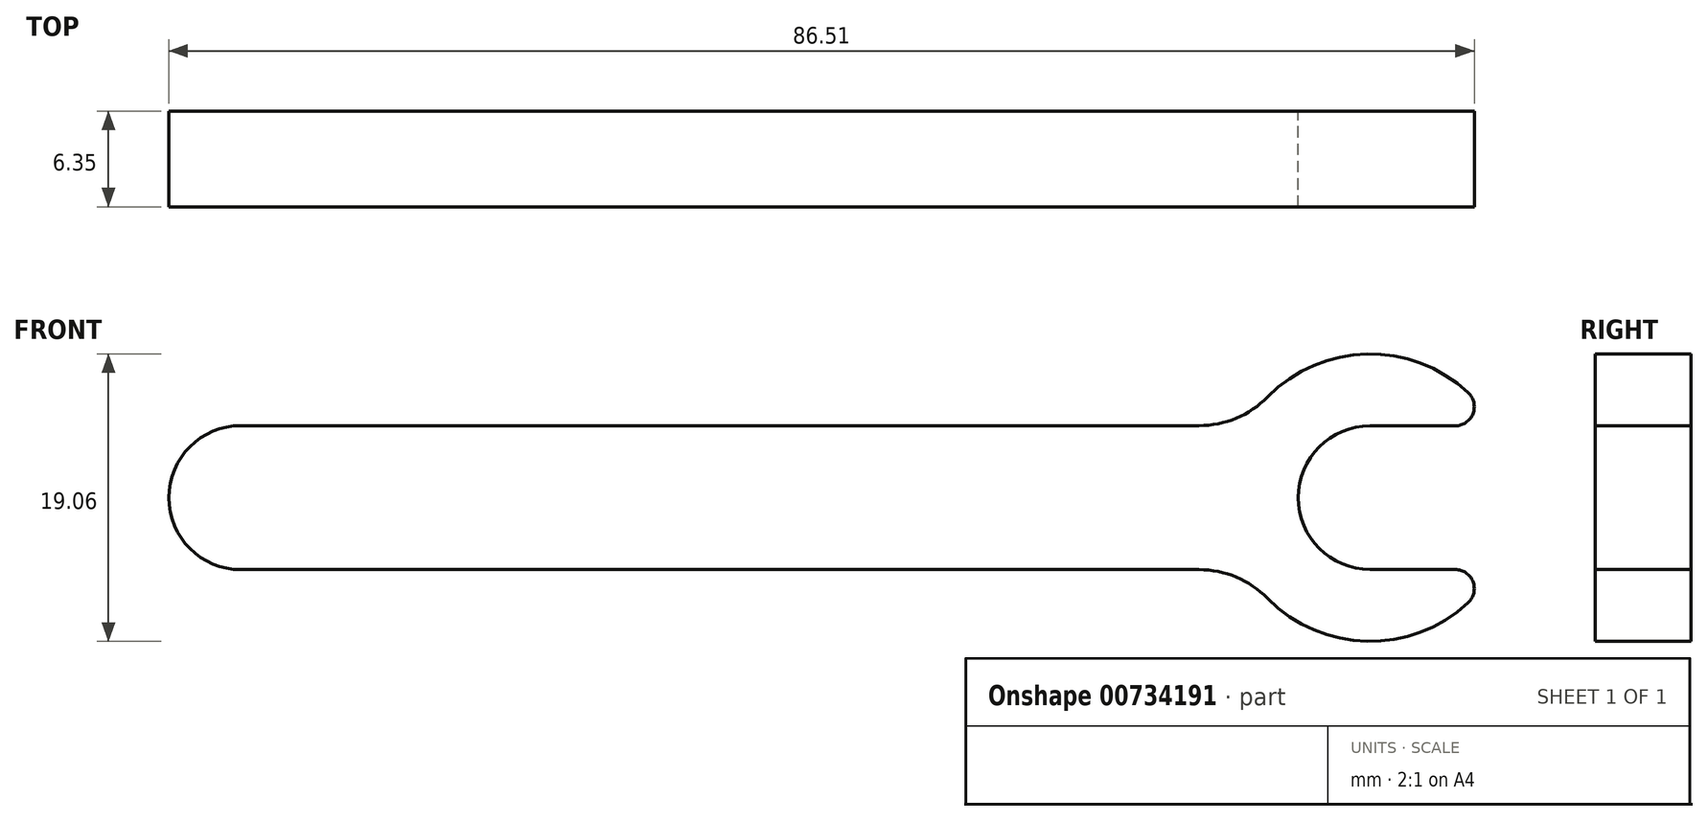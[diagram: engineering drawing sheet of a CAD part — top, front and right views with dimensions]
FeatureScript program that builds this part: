
annotation { "Feature Type Name" : "Feature", "Feature Type Description" : "" }
export const myFeature = defineFeature(function(context is Context, id is Id, definition is map)
    precondition{}
    {
        {
            var Q0;
            Q0=qCreatedBy(makeId("Front.planeOp"),FACE);
            var sketch = newSketch(context, id + "F0", { "sketchPlane" : qUnion([Q0])});
            skArc(sketch, "E0", {"start": v(0, 4.78) * mm, "mid": v(-4.78, 0) * mm, "end": v(0, -4.78) * mm});
            skLineSegment(sketch, "E1", {"start": v(0, 4.78) * mm, "end": v(63.5, 4.78) * mm});
            skLineSegment(sketch, "E2", {"start": v(0, -4.78) * mm, "end": v(63.5, -4.78) * mm});
            skArc(sketch, "E3", {"start": v(81.33, 6.96) * mm, "mid": v(74.62, 9.52) * mm, "end": v(68.03, 6.68) * mm});
            skPoint(sketch, "E4.visualSharp", {"position": v(66.58, 4.78) * mm});
            skArc(sketch, "E4.filletArc", {"start": v(63.5, 4.78) * mm, "mid": v(65.96, 5.27) * mm, "end": v(68.03, 6.68) * mm});
            skArc(sketch, "E5", {"start": v(68.03, -6.68) * mm, "mid": v(74.62, -9.52) * mm, "end": v(81.33, -6.96) * mm});
            skPoint(sketch, "E6.visualSharp", {"position": v(66.58, -4.78) * mm});
            skArc(sketch, "E6.filletArc", {"start": v(68.03, -6.68) * mm, "mid": v(65.96, -5.27) * mm, "end": v(63.5, -4.78) * mm});
            skArc(sketch, "E7", {"start": v(80.46, 4.76) * mm, "mid": v(81.64, 5.57) * mm, "end": v(81.33, 6.96) * mm});
            skArc(sketch, "E8", {"start": v(81.33, -6.96) * mm, "mid": v(81.64, -5.57) * mm, "end": v(80.46, -4.76) * mm});
            skLineSegment(sketch, "E9", {"start": v(80.46, 4.76) * mm, "end": v(74.82, 4.76) * mm});
            skLineSegment(sketch, "E10", {"start": v(80.46, -4.76) * mm, "end": v(74.82, -4.76) * mm});
            skArc(sketch, "E11", {"start": v(74.82, 4.76) * mm, "mid": v(70.06, 0) * mm, "end": v(74.82, -4.76) * mm});
            skSolve(sketch);
        }
        {
            var Q0;
            Q0=makeQuery(id+"F0.imprint","IMPRINT",FACE,{"disambiguationData":[TD([[makeQuery(id+"F0.imprint","IMPRINT",EDGE,{"derivedFrom":sQuery(id+"F0.wireOp",EDGE,"E0")}),1.0]])]});
            extrude(context, id + "F1", {"entities" : qUnion([Q0]), "depth" : 6.35 * mm, "offsetDistance" : 25.4 * mm});
        }
    });
